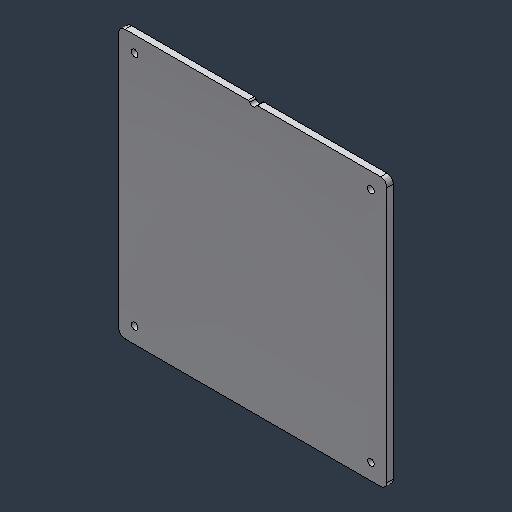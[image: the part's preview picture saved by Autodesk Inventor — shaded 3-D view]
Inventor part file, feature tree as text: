
AUTODESK INVENTOR PART (.ipt)
format: ipt  version: 2024.3 (Build 283343000, 343)  size: 94,208 bytes
history: native  units: mm (DEFAULTED — no unit token found)
features: fillet x1
ambient origin geometry x8: Origin, YZ Plane, XZ Plane, XY Plane, X Axis, Y Axis, Z Axis, Center Point
bodies: Solid1 (feature_tree)
feature tree (1):
  fillet  "Fillet2"  [1 undecoded]
note: 1 required parameter value undecoded (feature->parameter linkage not recoverable at this tier; creation-order binding heuristic only, values carry confidence <= 0.55)
